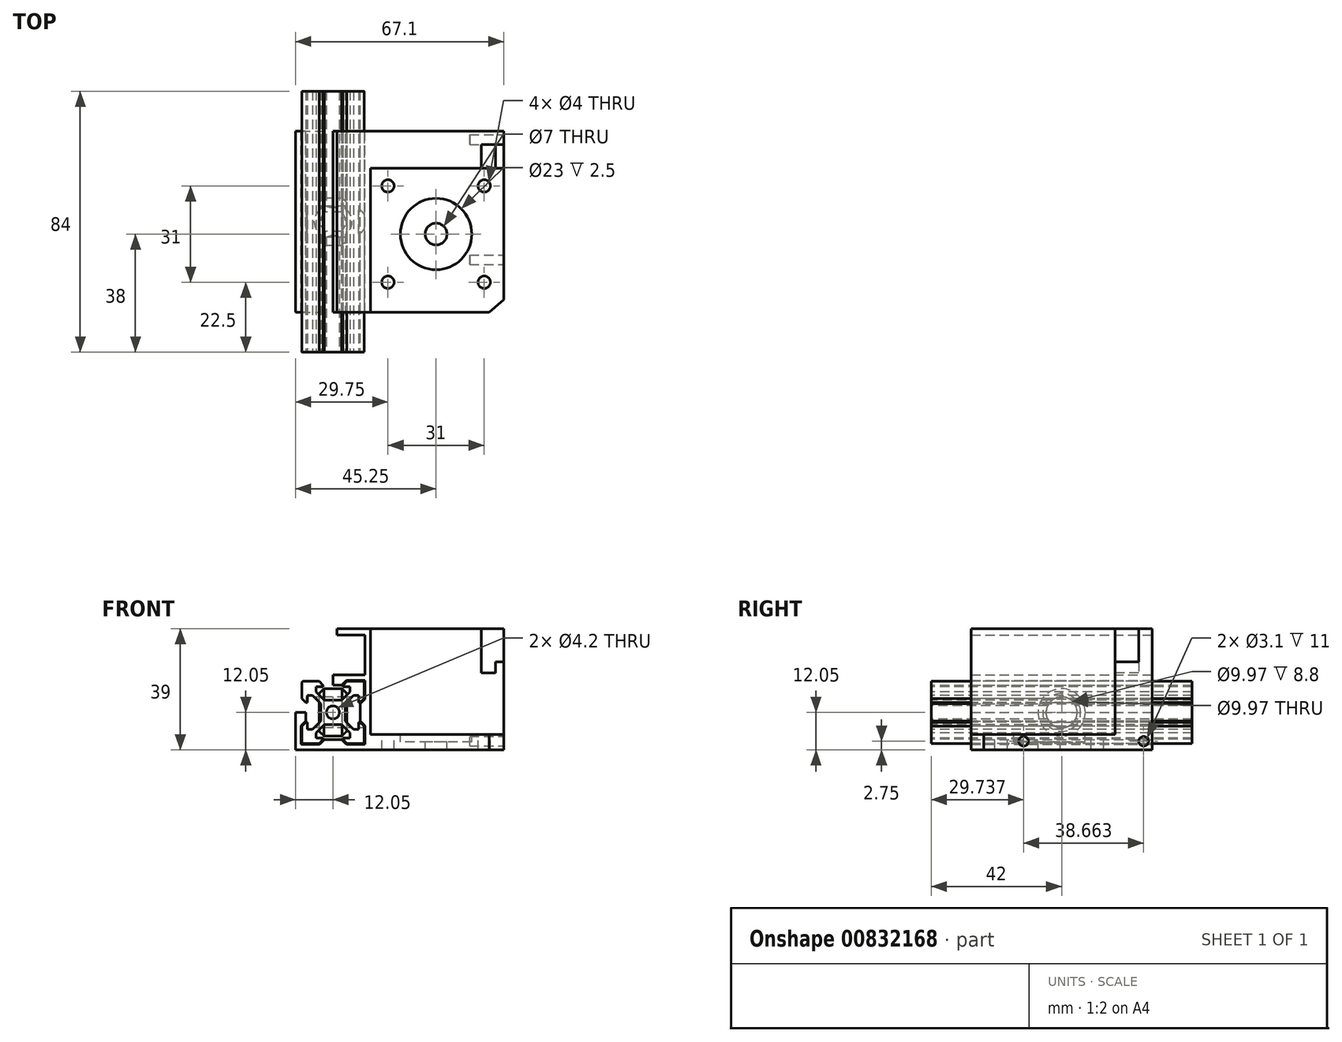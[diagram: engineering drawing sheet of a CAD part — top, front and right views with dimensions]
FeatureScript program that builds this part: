
annotation { "Feature Type Name" : "Feature", "Feature Type Description" : "" }
export const myFeature = defineFeature(function(context is Context, id is Id, definition is map)
    precondition{}
    {
        {
            var Q0;
            Q0=qCreatedBy(makeId("Front.planeOp"),FACE);
            var sketch = newSketch(context, id + "F0", { "sketchPlane" : qUnion([Q0])});
            skLineSegment(sketch, "E0", {"start": v(0, 3.9) * mm, "end": v(-2.84, 3.9) * mm});
            skLineSegment(sketch, "E1", {"start": v(-2.84, 3.9) * mm, "end": v(-5.5, 6.56) * mm});
            skLineSegment(sketch, "E2", {"start": v(-5.5, 6.56) * mm, "end": v(-5.5, 8.2) * mm});
            skLineSegment(sketch, "E3", {"start": v(-5.5, 8.2) * mm, "end": v(-3.15, 8.2) * mm});
            skLineSegment(sketch, "E4", {"start": v(-3.15, 8.7) * mm, "end": v(-4.46, 10) * mm});
            skLineSegment(sketch, "E5", {"start": v(-4.46, 10) * mm, "end": v(-10, 10) * mm});
            skLineSegment(sketch, "E6.MirrorCS", {"start": v(4.46, 10) * mm, "end": v(10, 10) * mm});
            skLineSegment(sketch, "E7.MirrorCS", {"start": v(5.5, 6.56) * mm, "end": v(5.5, 8.2) * mm});
            skLineSegment(sketch, "E8.MirrorCS", {"start": v(2.84, 3.9) * mm, "end": v(5.5, 6.56) * mm});
            skLineSegment(sketch, "E9.MirrorCS", {"start": v(0, 3.9) * mm, "end": v(2.84, 3.9) * mm});
            skLineSegment(sketch, "E10.MirrorCS", {"start": v(-10, 4.46) * mm, "end": v(-10, 10) * mm});
            skLineSegment(sketch, "E11.MirrorCS", {"start": v(-6.56, 5.5) * mm, "end": v(-8.2, 5.5) * mm});
            skLineSegment(sketch, "E12.MirrorCS", {"start": v(-3.9, 2.84) * mm, "end": v(-6.56, 5.5) * mm});
            skLineSegment(sketch, "E13.MirrorCS", {"start": v(10, 4.46) * mm, "end": v(10, 10) * mm});
            skLineSegment(sketch, "E14.MirrorCS", {"start": v(6.56, 5.5) * mm, "end": v(8.2, 5.5) * mm});
            skLineSegment(sketch, "E15.MirrorCS", {"start": v(3.9, 2.84) * mm, "end": v(6.56, 5.5) * mm});
            skLineSegment(sketch, "E16", {"start": v(-3.9, 2.84) * mm, "end": v(-3.9, 0) * mm});
            skLineSegment(sketch, "E17.MirrorCS", {"start": v(3.9, 2.84) * mm, "end": v(3.9, 0) * mm});
            skLineSegment(sketch, "E18.MirrorCS", {"start": v(-3.9, -2.84) * mm, "end": v(-3.9, 0) * mm});
            skLineSegment(sketch, "E19.MirrorCS", {"start": v(-3.9, -2.84) * mm, "end": v(-6.56, -5.5) * mm});
            skLineSegment(sketch, "E20.MirrorCS", {"start": v(-6.56, -5.5) * mm, "end": v(-8.2, -5.5) * mm});
            skLineSegment(sketch, "E21.MirrorCS", {"start": v(-10, -4.46) * mm, "end": v(-10, -10) * mm});
            skLineSegment(sketch, "E22.MirrorCS", {"start": v(-4.46, -10) * mm, "end": v(-10, -10) * mm});
            skLineSegment(sketch, "E23.MirrorCS", {"start": v(-5.5, -6.56) * mm, "end": v(-5.5, -8.2) * mm});
            skLineSegment(sketch, "E24.MirrorCS", {"start": v(-2.84, -3.9) * mm, "end": v(-5.5, -6.56) * mm});
            skLineSegment(sketch, "E25.MirrorCS", {"start": v(0, -3.9) * mm, "end": v(-2.84, -3.9) * mm});
            skLineSegment(sketch, "E26.MirrorCS", {"start": v(0, -3.9) * mm, "end": v(2.84, -3.9) * mm});
            skLineSegment(sketch, "E27.MirrorCS", {"start": v(2.84, -3.9) * mm, "end": v(5.5, -6.56) * mm});
            skLineSegment(sketch, "E28.MirrorCS", {"start": v(5.5, -6.56) * mm, "end": v(5.5, -8.2) * mm});
            skLineSegment(sketch, "E29.MirrorCS", {"start": v(4.46, -10) * mm, "end": v(10, -10) * mm});
            skLineSegment(sketch, "E30.MirrorCS", {"start": v(10, -4.46) * mm, "end": v(10, -10) * mm});
            skLineSegment(sketch, "E31.MirrorCS", {"start": v(6.56, -5.5) * mm, "end": v(8.2, -5.5) * mm});
            skLineSegment(sketch, "E32.MirrorCS", {"start": v(3.9, -2.84) * mm, "end": v(6.56, -5.5) * mm});
            skLineSegment(sketch, "E33.MirrorCS", {"start": v(3.9, -2.84) * mm, "end": v(3.9, 0) * mm});
            skLineSegment(sketch, "E34", {"start": v(-3.15, 8.2) * mm, "end": v(-3.15, 8.7) * mm});
            skPoint(sketch, "E35.MirrorCS.end.orphan", {"position": v(4.46, 10) * mm});
            skPoint(sketch, "E36.MirrorCS.start.orphan", {"position": v(5.5, 8.2) * mm});
            skLineSegment(sketch, "E37.MirrorCS", {"start": v(3.15, 8.7) * mm, "end": v(4.46, 10) * mm});
            skLineSegment(sketch, "E38.MirrorCS", {"start": v(3.15, 8.2) * mm, "end": v(3.15, 8.7) * mm});
            skLineSegment(sketch, "E39.MirrorCS", {"start": v(5.5, 8.2) * mm, "end": v(3.15, 8.2) * mm});
            skLineSegment(sketch, "E40.MirrorCS", {"start": v(-8.7, 3.15) * mm, "end": v(-10, 4.46) * mm});
            skLineSegment(sketch, "E41.MirrorCS", {"start": v(-8.2, 3.15) * mm, "end": v(-8.7, 3.15) * mm});
            skLineSegment(sketch, "E42.MirrorCS", {"start": v(-8.2, 5.5) * mm, "end": v(-8.2, 3.15) * mm});
            skLineSegment(sketch, "E43.MirrorCS", {"start": v(-8.2, -5.5) * mm, "end": v(-8.2, -3.15) * mm});
            skLineSegment(sketch, "E44.MirrorCS", {"start": v(-8.2, -3.15) * mm, "end": v(-8.7, -3.15) * mm});
            skLineSegment(sketch, "E45.MirrorCS", {"start": v(-8.7, -3.15) * mm, "end": v(-10, -4.46) * mm});
            skLineSegment(sketch, "E46.MirrorCS", {"start": v(-5.5, -8.2) * mm, "end": v(-3.15, -8.2) * mm});
            skLineSegment(sketch, "E47.MirrorCS", {"start": v(-3.15, -8.2) * mm, "end": v(-3.15, -8.7) * mm});
            skLineSegment(sketch, "E48.MirrorCS", {"start": v(-3.15, -8.7) * mm, "end": v(-4.46, -10) * mm});
            skLineSegment(sketch, "E49.MirrorCS", {"start": v(8.2, 5.5) * mm, "end": v(8.2, 3.15) * mm});
            skLineSegment(sketch, "E50.MirrorCS", {"start": v(8.2, 3.15) * mm, "end": v(8.7, 3.15) * mm});
            skLineSegment(sketch, "E51.MirrorCS", {"start": v(8.7, 3.15) * mm, "end": v(10, 4.46) * mm});
            skLineSegment(sketch, "E52.MirrorCS", {"start": v(3.15, -8.2) * mm, "end": v(3.15, -8.7) * mm});
            skLineSegment(sketch, "E53.MirrorCS", {"start": v(3.15, -8.7) * mm, "end": v(4.46, -10) * mm});
            skLineSegment(sketch, "E54.MirrorCS", {"start": v(5.5, -8.2) * mm, "end": v(3.15, -8.2) * mm});
            skLineSegment(sketch, "E55.MirrorCS", {"start": v(8.2, -5.5) * mm, "end": v(8.2, -3.15) * mm});
            skLineSegment(sketch, "E56.MirrorCS", {"start": v(8.2, -3.15) * mm, "end": v(8.7, -3.15) * mm});
            skLineSegment(sketch, "E57.MirrorCS", {"start": v(8.7, -3.15) * mm, "end": v(10, -4.46) * mm});
            skCircle(sketch, "E58", {"center": v(0, 0) * mm, "radius": 2.1 * mm});
            skSolve(sketch);
        }
        {
            var Q0;
            Q0=makeQuery(id+"F0.imprint","IMPRINT",FACE,{"disambiguationData":[TD([[makeQuery(id+"F0.imprint","IMPRINT",EDGE,{"derivedFrom":sQuery(id+"F0.wireOp",EDGE,"E0")}),1.0]])]});
            extrude(context, id + "F1", {"entities" : qUnion([Q0]), "endBound" : BoundingType.SYMMETRIC, "oppositeDirection" : true, "depth" : 84 * mm, "offsetDistance" : 25 * mm});
        }
        {
            var Q0;
            Q0=makeQuery(id+"F1.opExtrude","SWEPT_EDGE",EDGE,{"disambiguationData":[OSD([sQuery(id+"F0.wireOp",EDGE,"E6.MirrorCS"),sQuery(id+"F0.wireOp",EDGE,"E13.MirrorCS")])]});
            var Q1;
            Q1=makeQuery(id+"F1.opExtrude","SWEPT_EDGE",EDGE,{"disambiguationData":[OSD([sQuery(id+"F0.wireOp",EDGE,"E5"),sQuery(id+"F0.wireOp",EDGE,"E10.MirrorCS")])]});
            var Q2;
            Q2=makeQuery(id+"F1.opExtrude","SWEPT_EDGE",EDGE,{"disambiguationData":[OSD([sQuery(id+"F0.wireOp",EDGE,"E29.MirrorCS"),sQuery(id+"F0.wireOp",EDGE,"E30.MirrorCS")])]});
            var Q3;
            Q3=makeQuery(id+"F1.opExtrude","SWEPT_EDGE",EDGE,{"disambiguationData":[OSD([sQuery(id+"F0.wireOp",EDGE,"E21.MirrorCS"),sQuery(id+"F0.wireOp",EDGE,"E22.MirrorCS")])]});
            fillet(context, id + "F2", {"entities" : qUnion([Q0, Q1, Q2, Q3]), "radius" : .5 * mm, "tangentPropagation" : true, "allowEdgeOverflow" : false});
        }
        {
            var Q0;
            Q0=qCreatedBy(makeId("Front.planeOp"),FACE);
            var sketch = newSketch(context, id + "F3", { "sketchPlane" : qUnion([Q0])});
            skLineSegment(sketch, "E59.bottom", {"start": v(2.89, -7.62) * mm, "end": v(-2.89, -7.61) * mm});
            skLineSegment(sketch, "E59.top", {"start": v(2.89, 7.61) * mm, "end": v(-2.89, 7.62) * mm});
            skLineSegment(sketch, "E59.left", {"start": v(4.4, -6.1) * mm, "end": v(4.4, 6.1) * mm});
            skLineSegment(sketch, "E59.right", {"start": v(-4.4, -6.1) * mm, "end": v(-4.4, 6.1) * mm});
            skPoint(sketch, "E59.middle", {"position": v(0, 0) * mm});
            skLineSegment(sketch, "E60", {"start": v(-4.4, 6.1) * mm, "end": v(-2.89, 7.62) * mm});
            skLineSegment(sketch, "E61.MirrorCS", {"start": v(4.4, 6.1) * mm, "end": v(2.89, 7.62) * mm});
            skLineSegment(sketch, "E62.MirrorCS", {"start": v(-4.4, -6.1) * mm, "end": v(-2.89, -7.62) * mm});
            skLineSegment(sketch, "E63.MirrorCS", {"start": v(4.4, -6.1) * mm, "end": v(2.89, -7.62) * mm});
            skLineSegment(sketch, "E64", {"start": v(-4.4, 0) * mm, "end": v(0, 0) * mm});
            skLineSegment(sketch, "E65", {"start": v(4.4, 0) * mm, "end": v(0, 0) * mm});
            skSolve(sketch);
        }
        {
            var Q0;
            Q0=makeQuery(id+"F3.imprint","IMPRINT",FACE,{"disambiguationData":[TD([[makeQuery(id+"F3.imprint","IMPRINT",EDGE,{"derivedFrom":sQuery(id+"F3.wireOp",EDGE,"E59.top")}),1.0]])]});
            var Q1;
            Q1=sQuery(id+"F3.wireOp",EDGE,"E65");
            revolve(context, id + "F4", {"surfaceOperationType" : NewSurfaceOperationType.NEW, "entities" : qUnion([Q0]), "axis" : qUnion([Q1]), "revolveType" : RevolveType.FULL});
        }
        {
            var Q0;
            Q0=makeQuery(id+"F4.opRevolve","SWEPT_FACE",FACE,{"disambiguationData":[OSD([sQuery(id+"F3.wireOp",EDGE,"E59.left")])]});
            var sketch = newSketch(context, id + "F5", { "sketchPlane" : qUnion([Q0])});
            skCircle(sketch, "E66", {"center": v(0, 0) * mm, "radius": 4.99 * mm});
            skSolve(sketch);
        }
        {
            var Q0;
            Q0=makeQuery(id+"F5.imprint","IMPRINT",FACE,{"disambiguationData":[TD([[makeQuery(id+"F5.imprint","IMPRINT",EDGE,{"derivedFrom":sQuery(id+"F5.wireOp",EDGE,"E66")}),1.0]])]});
            var Q1;
            Q1=sQuery(id+"F5.wireOp",EDGE,"E66");
            extrude(context, id + "F6", {"entities" : qUnion([Q0]), "operationType" : NewBodyOperationType.REMOVE, "surfaceEntities" : qUnion([Q1]), "endBound" : BoundingType.SYMMETRIC, "depth" : 25.8 * mm, "offsetDistance" : 25 * mm});
        }
        {
            var Q0;
            Q0=qCreatedBy(makeId("Front.planeOp"),FACE);
            var sketch = newSketch(context, id + "F7", { "sketchPlane" : qUnion([Q0])});
            skLineSegment(sketch, "E67", {"start": v(-4.33, -10.3) * mm, "end": v(-2.83, -8.8) * mm});
            skLineSegment(sketch, "E68", {"start": v(-2.83, -8.8) * mm, "end": v(0, -8.8) * mm});
            skLineSegment(sketch, "E69", {"start": v(0, -8.8) * mm, "end": v(0, -12.05) * mm});
            skLineSegment(sketch, "E70", {"start": v(0, -12.05) * mm, "end": v(-12.05, -12.05) * mm});
            skLineSegment(sketch, "E71", {"start": v(-12.05, -12.05) * mm, "end": v(-12.05, 0) * mm});
            skLineSegment(sketch, "E72", {"start": v(-12.05, 0) * mm, "end": v(-8.8, 0) * mm});
            skLineSegment(sketch, "E73", {"start": v(-8.8, 0) * mm, "end": v(-8.8, -2.83) * mm});
            skLineSegment(sketch, "E74", {"start": v(-8.8, -2.83) * mm, "end": v(-10.3, -4.33) * mm});
            skLineSegment(sketch, "E75", {"start": v(-10.3, -4.33) * mm, "end": v(-10.3, -10.3) * mm});
            skLineSegment(sketch, "E76", {"start": v(-10.3, -10.3) * mm, "end": v(-4.33, -10.3) * mm});
            skLineSegment(sketch, "E77.MirrorCS", {"start": v(0, -12.05) * mm, "end": v(12.05, -12.05) * mm});
            skLineSegment(sketch, "E78.MirrorCS", {"start": v(2.83, -8.8) * mm, "end": v(0, -8.8) * mm});
            skLineSegment(sketch, "E79.MirrorCS", {"start": v(4.33, -10.3) * mm, "end": v(2.83, -8.8) * mm});
            skLineSegment(sketch, "E80.MirrorCS", {"start": v(10.3, -10.3) * mm, "end": v(4.33, -10.3) * mm});
            skLineSegment(sketch, "E81.MirrorCS", {"start": v(10.3, -4.33) * mm, "end": v(10.3, -10.3) * mm});
            skLineSegment(sketch, "E82.MirrorCS", {"start": v(12.05, -12.05) * mm, "end": v(12.05, 0) * mm});
            skLineSegment(sketch, "E83.MirrorCS", {"start": v(12.05, 0) * mm, "end": v(8.8, 0) * mm});
            skLineSegment(sketch, "E84.MirrorCS", {"start": v(8.8, 0) * mm, "end": v(8.8, -2.83) * mm});
            skLineSegment(sketch, "E85.MirrorCS", {"start": v(12.05, 12.05) * mm, "end": v(12.05, 0) * mm});
            skLineSegment(sketch, "E86.MirrorCS", {"start": v(8.8, -2.83) * mm, "end": v(10.3, -4.33) * mm});
            skLineSegment(sketch, "E87.MirrorCS", {"start": v(8.8, 0) * mm, "end": v(8.8, 2.83) * mm});
            skLineSegment(sketch, "E88.MirrorCS", {"start": v(8.8, 2.83) * mm, "end": v(10.3, 4.33) * mm});
            skLineSegment(sketch, "E89.MirrorCS", {"start": v(10.3, 4.33) * mm, "end": v(10.3, 10.3) * mm});
            skLineSegment(sketch, "E90.MirrorCS", {"start": v(10.3, 10.3) * mm, "end": v(4.33, 10.3) * mm});
            skLineSegment(sketch, "E91.MirrorCS", {"start": v(4.33, 10.3) * mm, "end": v(2.83, 8.8) * mm});
            skLineSegment(sketch, "E92.MirrorCS", {"start": v(2.83, 8.8) * mm, "end": v(0, 8.8) * mm});
            skLineSegment(sketch, "E93.MirrorCS", {"start": v(0, 8.8) * mm, "end": v(0, 12.05) * mm});
            skLineSegment(sketch, "E94.MirrorCS", {"start": v(0, 12.05) * mm, "end": v(12.05, 12.05) * mm});
            skLineSegment(sketch, "E95", {"start": v(10.3, 12.05) * mm, "end": v(10.3, 26.95) * mm});
            skLineSegment(sketch, "E96", {"start": v(12.05, 12.05) * mm, "end": v(12.05, 26.95) * mm});
            skLineSegment(sketch, "E97", {"start": v(12.05, 26.95) * mm, "end": v(10.3, 26.95) * mm});
            skLineSegment(sketch, "E98", {"start": v(12.05, -12.05) * mm, "end": v(55.05, -12.05) * mm});
            skLineSegment(sketch, "E99", {"start": v(55.05, -12.05) * mm, "end": v(55.05, -7.05) * mm});
            skLineSegment(sketch, "E100", {"start": v(55.05, -7.05) * mm, "end": v(12.05, -7.05) * mm});
            skLineSegment(sketch, "E101", {"start": v(10.3, 26.95) * mm, "end": v(1.3, 26.95) * mm});
            skLineSegment(sketch, "E102", {"start": v(1.3, 26.95) * mm, "end": v(1.3, 24.95) * mm});
            skLineSegment(sketch, "E103", {"start": v(1.3, 24.95) * mm, "end": v(10.3, 24.95) * mm});
            skLineSegment(sketch, "E104", {"start": v(12.05, 26.95) * mm, "end": v(47.8, 26.95) * mm});
            skLineSegment(sketch, "E105", {"start": v(55.05, 26.95) * mm, "end": v(55.05, 16.25) * mm});
            skLineSegment(sketch, "E106", {"start": v(47.8, 26.95) * mm, "end": v(47.8, 12.75) * mm});
            skLineSegment(sketch, "E107", {"start": v(47.8, 12.75) * mm, "end": v(52.3, 12.75) * mm});
            skLineSegment(sketch, "E108", {"start": v(55.05, 16.25) * mm, "end": v(52.3, 16.25) * mm});
            skLineSegment(sketch, "E109", {"start": v(52.3, 16.25) * mm, "end": v(52.3, 12.75) * mm});
            skLineSegment(sketch, "E110", {"start": v(47.8, 26.95) * mm, "end": v(55.05, 26.95) * mm});
            skLineSegment(sketch, "E111", {"start": v(55.05, 16.25) * mm, "end": v(55.05, -7.05) * mm});
            skLineSegment(sketch, "E112", {"start": v(52.3, 12.75) * mm, "end": v(55.05, 12.75) * mm});
            skSolve(sketch);
        }
        {
            var Q0;
            Q0=makeQuery(id+"F7.imprint","IMPRINT",FACE,{"disambiguationData":[TD([[makeQuery(id+"F7.imprint","IMPRINT",EDGE,{"derivedFrom":sQuery(id+"F7.wireOp",EDGE,"E83.MirrorCS")}),-1.0]])]});
            var Q1;
            Q1=makeQuery(id+"F7.imprint","IMPRINT",FACE,{"disambiguationData":[TD([[makeQuery(id+"F7.imprint","IMPRINT",EDGE,{"derivedFrom":sQuery(id+"F7.wireOp",EDGE,"E69")}),1.0]])]});
            var Q2;
            Q2=makeQuery(id+"F7.imprint","IMPRINT",FACE,{"disambiguationData":[TD([[makeQuery(id+"F7.imprint","IMPRINT",EDGE,{"derivedFrom":sQuery(id+"F7.wireOp",EDGE,"E67")}),-1.0]])]});
            var Q3;
            {var subQ0=sQuery(id+"F7.wireOp",EDGE,"E96");Q3=makeQuery(id+"F7.imprint","IMPRINT",FACE,{"disambiguationData":[TD([[makeQuery(id+"F7.imprint","IMPRINT",EDGE,{"derivedFrom":subQ0}),1.0]])]});}
            var Q4;
            {var subQ0=sQuery(id+"F7.wireOp",EDGE,"E101");Q4=makeQuery(id+"F7.imprint","IMPRINT",FACE,{"disambiguationData":[TD([[makeQuery(id+"F7.imprint","IMPRINT",EDGE,{"derivedFrom":subQ0}),1.0]])]});}
            var Q5;
            {var subQ0=sQuery(id+"F7.wireOp",EDGE,"E98");Q5=makeQuery(id+"F7.imprint","IMPRINT",FACE,{"disambiguationData":[TD([[makeQuery(id+"F7.imprint","IMPRINT",EDGE,{"derivedFrom":subQ0}),1.0]])]});}
            extrude(context, id + "F8", {"entities" : qUnion([Q0, Q1, Q2, Q3, Q4, Q5]), "endBound" : BoundingType.SYMMETRIC, "depth" : 58.3 * mm, "offsetDistance" : 25 * mm});
        }
        {
            var Q0;
            Q0=qCreatedBy(makeId("Right.planeOp"),FACE);
            var sketch = newSketch(context, id + "F9", { "sketchPlane" : qUnion([Q0])});
            skLineSegment(sketch, "E113", {"start": v(29.15, 26.95) * mm, "end": v(17.15, 26.95) * mm});
            skLineSegment(sketch, "E114", {"start": v(17.15, 26.95) * mm, "end": v(17.15, -7.05) * mm});
            skLineSegment(sketch, "E115", {"start": v(17.15, -7.05) * mm, "end": v(29.15, -7.05) * mm});
            skLineSegment(sketch, "E116", {"start": v(29.15, -7.05) * mm, "end": v(29.15, 26.95) * mm});
            skSolve(sketch);
        }
        {
            var Q0;
            Q0=makeQuery(id+"F9.imprint","IMPRINT",FACE,{"disambiguationData":[TD([[makeQuery(id+"F9.imprint","IMPRINT",EDGE,{"derivedFrom":sQuery(id+"F9.wireOp",EDGE,"E113")}),1.0]])]});
            extrude(context, id + "F10", {"entities" : qUnion([Q0]), "operationType" : NewBodyOperationType.ADD, "depth" : 55.05 * mm, "offsetDistance" : 25 * mm, "hasSecondDirection" : true, "secondDirectionOppositeDirection" : false, "secondDirectionDepth" : 12 * mm});
        }
        {
            var Q0;
            Q0=qCreatedBy(makeId("Top.planeOp"),FACE);
            var sketch = newSketch(context, id + "F11", { "sketchPlane" : qUnion([Q0])});
            skCircle(sketch, "E117", {"center": v(33.2, -4) * mm, "radius": 3.5 * mm});
            skCircle(sketch, "E118", {"center": v(33.2, -4) * mm, "radius": 11.5 * mm});
            skCircle(sketch, "E119", {"center": v(17.7, 11.5) * mm, "radius": 2 * mm});
            skCircle(sketch, "E120", {"center": v(48.7, 11.5) * mm, "radius": 2 * mm});
            skCircle(sketch, "E121", {"center": v(48.7, -19.5) * mm, "radius": 2 * mm});
            skCircle(sketch, "E122", {"center": v(17.7, -19.5) * mm, "radius": 2 * mm});
            skSolve(sketch);
        }
        {
            var Q0;
            Q0=sQuery(id+"F11.wireOp",VERTEX,"E122.center");
            var Q1;
            Q1=sQuery(id+"F11.wireOp",VERTEX,"E121.center");
            var Q2;
            Q2=sQuery(id+"F11.wireOp",VERTEX,"E120.center");
            var Q3;
            Q3=sQuery(id+"F11.wireOp",VERTEX,"E119.center");
            var Q4;
            Q4=makeQuery(id+"F8.opExtrude","SWEPT_BODY",BODY,{"disambiguationData":[OSD([sQuery(id+"F7.wireOp",EDGE,"E67"),sQuery(id+"F7.wireOp",EDGE,"E68"),sQuery(id+"F7.wireOp",EDGE,"E70"),sQuery(id+"F7.wireOp",EDGE,"E71"),sQuery(id+"F7.wireOp",EDGE,"E72"),sQuery(id+"F7.wireOp",EDGE,"E73"),sQuery(id+"F7.wireOp",EDGE,"E74"),sQuery(id+"F7.wireOp",EDGE,"E75"),sQuery(id+"F7.wireOp",EDGE,"E76"),sQuery(id+"F7.wireOp",EDGE,"E77.MirrorCS"),sQuery(id+"F7.wireOp",EDGE,"E78.MirrorCS"),sQuery(id+"F7.wireOp",EDGE,"E79.MirrorCS"),sQuery(id+"F7.wireOp",EDGE,"E80.MirrorCS"),sQuery(id+"F7.wireOp",EDGE,"E81.MirrorCS"),sQuery(id+"F7.wireOp",EDGE,"E82.MirrorCS"),sQuery(id+"F7.wireOp",EDGE,"E84.MirrorCS"),sQuery(id+"F7.wireOp",EDGE,"E85.MirrorCS"),sQuery(id+"F7.wireOp",EDGE,"E86.MirrorCS"),sQuery(id+"F7.wireOp",EDGE,"E87.MirrorCS"),sQuery(id+"F7.wireOp",EDGE,"E88.MirrorCS"),sQuery(id+"F7.wireOp",EDGE,"E89.MirrorCS"),sQuery(id+"F7.wireOp",EDGE,"E90.MirrorCS"),sQuery(id+"F7.wireOp",EDGE,"E91.MirrorCS"),sQuery(id+"F7.wireOp",EDGE,"E92.MirrorCS"),sQuery(id+"F7.wireOp",EDGE,"E93.MirrorCS"),sQuery(id+"F7.wireOp",EDGE,"E94.MirrorCS"),sQuery(id+"F7.wireOp",EDGE,"E95"),sQuery(id+"F7.wireOp",EDGE,"E96"),sQuery(id+"F7.wireOp",EDGE,"E97"),sQuery(id+"F7.wireOp",EDGE,"E98"),sQuery(id+"F7.wireOp",EDGE,"E99"),sQuery(id+"F7.wireOp",EDGE,"E100"),sQuery(id+"F7.wireOp",EDGE,"E101"),sQuery(id+"F7.wireOp",EDGE,"E102"),sQuery(id+"F7.wireOp",EDGE,"E103")])]});
            hole(context, id + "F12", {"style" : HoleStyle.SIMPLE, "endStyle" : HoleEndStyle.THROUGH, "holeDiameter" : 4 * mm, "majorDiameter" : 5 * mm, "isTappedThrough" : true, "tappedDepth" : 12 * mm, "tapClearance" : 3, "locations" : qUnion([Q0, Q1, Q2, Q3]), "scope" : qUnion([Q4])});
        }
        {
            var Q0;
            Q0=sQuery(id+"F11.wireOp",VERTEX,"E117.center");
            var Q1;
            Q1=makeQuery(id+"F8.opExtrude","SWEPT_BODY",BODY,{"disambiguationData":[OSD([sQuery(id+"F7.wireOp",EDGE,"E67"),sQuery(id+"F7.wireOp",EDGE,"E68"),sQuery(id+"F7.wireOp",EDGE,"E70"),sQuery(id+"F7.wireOp",EDGE,"E71"),sQuery(id+"F7.wireOp",EDGE,"E72"),sQuery(id+"F7.wireOp",EDGE,"E73"),sQuery(id+"F7.wireOp",EDGE,"E74"),sQuery(id+"F7.wireOp",EDGE,"E75"),sQuery(id+"F7.wireOp",EDGE,"E76"),sQuery(id+"F7.wireOp",EDGE,"E77.MirrorCS"),sQuery(id+"F7.wireOp",EDGE,"E78.MirrorCS"),sQuery(id+"F7.wireOp",EDGE,"E79.MirrorCS"),sQuery(id+"F7.wireOp",EDGE,"E80.MirrorCS"),sQuery(id+"F7.wireOp",EDGE,"E81.MirrorCS"),sQuery(id+"F7.wireOp",EDGE,"E82.MirrorCS"),sQuery(id+"F7.wireOp",EDGE,"E84.MirrorCS"),sQuery(id+"F7.wireOp",EDGE,"E85.MirrorCS"),sQuery(id+"F7.wireOp",EDGE,"E86.MirrorCS"),sQuery(id+"F7.wireOp",EDGE,"E87.MirrorCS"),sQuery(id+"F7.wireOp",EDGE,"E88.MirrorCS"),sQuery(id+"F7.wireOp",EDGE,"E89.MirrorCS"),sQuery(id+"F7.wireOp",EDGE,"E90.MirrorCS"),sQuery(id+"F7.wireOp",EDGE,"E91.MirrorCS"),sQuery(id+"F7.wireOp",EDGE,"E92.MirrorCS"),sQuery(id+"F7.wireOp",EDGE,"E93.MirrorCS"),sQuery(id+"F7.wireOp",EDGE,"E94.MirrorCS"),sQuery(id+"F7.wireOp",EDGE,"E95"),sQuery(id+"F7.wireOp",EDGE,"E96"),sQuery(id+"F7.wireOp",EDGE,"E97"),sQuery(id+"F7.wireOp",EDGE,"E98"),sQuery(id+"F7.wireOp",EDGE,"E99"),sQuery(id+"F7.wireOp",EDGE,"E100"),sQuery(id+"F7.wireOp",EDGE,"E101"),sQuery(id+"F7.wireOp",EDGE,"E102"),sQuery(id+"F7.wireOp",EDGE,"E103")])]});
            hole(context, id + "F13", {"style" : HoleStyle.C_BORE, "endStyle" : HoleEndStyle.THROUGH, "holeDiameter" : 7 * mm, "cBoreDiameter" : 23 * mm, "cBoreDepth" : 2.5 * mm, "majorDiameter" : 5 * mm, "isTappedThrough" : true, "tappedDepth" : 12 * mm, "tapClearance" : 3, "locations" : qUnion([Q0]), "scope" : qUnion([Q1])});
        }
        {
            var Q0;
            Q0=makeQuery(id+"F10.opExtrude","SWEPT_FACE",FACE,{"disambiguationData":[OSD([sQuery(id+"F9.wireOp",EDGE,"E114")])]});
            var sketch = newSketch(context, id + "F14", { "sketchPlane" : qUnion([Q0])});
            skLineSegment(sketch, "E123", {"start": v(47.8, 26.95) * mm, "end": v(47.8, 12.75) * mm});
            skLineSegment(sketch, "E124", {"start": v(47.8, 12.75) * mm, "end": v(52.3, 12.75) * mm});
            skLineSegment(sketch, "E125", {"start": v(52.3, 12.75) * mm, "end": v(52.3, 16.25) * mm});
            skLineSegment(sketch, "E126", {"start": v(52.3, 16.25) * mm, "end": v(55.05, 16.25) * mm});
            skLineSegment(sketch, "E127", {"start": v(55.05, 16.25) * mm, "end": v(55.05, 26.95) * mm});
            skLineSegment(sketch, "E128", {"start": v(55.05, 26.95) * mm, "end": v(47.8, 26.95) * mm});
            skSolve(sketch);
        }
        {
            var Q0;
            Q0=makeQuery(id+"F14.imprint","IMPRINT",FACE,{"disambiguationData":[TD([[makeQuery(id+"F14.imprint","IMPRINT",EDGE,{"derivedFrom":sQuery(id+"F14.wireOp",EDGE,"E123")}),1.0]])]});
            extrude(context, id + "F15", {"entities" : qUnion([Q0]), "operationType" : NewBodyOperationType.REMOVE, "depth" : 0 * mm, "offsetDistance" : 25 * mm, "hasSecondDirection" : true, "secondDirectionOppositeDirection" : true, "secondDirectionDepth" : 7.67 * mm});
        }
        {
            var Q0;
            Q0=makeQuery(id+"F10.boolean.opBoolean","MERGE",FACE,{"derivedFrom":[makeQuery(id+"F8.opExtrude","SWEPT_FACE",FACE,{"disambiguationData":[OSD([sQuery(id+"F7.wireOp",EDGE,"E99")])]}),makeQuery(id+"F10.opExtrude","CAP_FACE",FACE,{"disambiguationData":[OSD([sQuery(id+"F9.wireOp",EDGE,"E113"),sQuery(id+"F9.wireOp",EDGE,"E114"),sQuery(id+"F9.wireOp",EDGE,"E115"),sQuery(id+"F9.wireOp",EDGE,"E116")])],"isStart":false})]});
            var sketch = newSketch(context, id + "F16", { "sketchPlane" : qUnion([Q0])});
            skCircle(sketch, "E129", {"center": v(-12.26, -9.3) * mm, "radius": 1.55 * mm});
            skCircle(sketch, "E130", {"center": v(26.4, -9.3) * mm, "radius": 1.55 * mm});
            skSolve(sketch);
        }
        {
            var Q0;
            Q0=makeQuery(id+"F16.imprint","IMPRINT",FACE,{"disambiguationData":[TD([[makeQuery(id+"F16.imprint","IMPRINT",EDGE,{"derivedFrom":sQuery(id+"F16.wireOp",EDGE,"E129")}),1.0]])]});
            var Q1;
            Q1=makeQuery(id+"F16.imprint","IMPRINT",FACE,{"disambiguationData":[TD([[makeQuery(id+"F16.imprint","IMPRINT",EDGE,{"derivedFrom":sQuery(id+"F16.wireOp",EDGE,"E130")}),1.0]])]});
            var Q2;
            Q2=sQuery(id+"F16.wireOp",EDGE,"E129");
            var Q3;
            Q3=sQuery(id+"F16.wireOp",EDGE,"E130");
            extrude(context, id + "F17", {"entities" : qUnion([Q0, Q1]), "operationType" : NewBodyOperationType.REMOVE, "surfaceEntities" : qUnion([Q2, Q3]), "oppositeDirection" : true, "depth" : 11 * mm, "offsetDistance" : 25 * mm});
        }
        {
            var Q0;
            Q0=makeQuery(id+"F8.opExtrude","SWEPT_FACE",FACE,{"disambiguationData":[OSD([sQuery(id+"F7.wireOp",EDGE,"E100")])]});
            var sketch = newSketch(context, id + "F18", { "sketchPlane" : qUnion([Q0])});
            skLineSegment(sketch, "E131", {"start": v(50.33, -29.15) * mm, "end": v(55.05, -25.13) * mm});
            skLineSegment(sketch, "E132", {"start": v(55.05, -25.13) * mm, "end": v(55.05, -29.15) * mm});
            skLineSegment(sketch, "E133", {"start": v(55.05, -29.15) * mm, "end": v(50.33, -29.15) * mm});
            skSolve(sketch);
        }
        {
            var Q0;
            Q0=makeQuery(id+"F18.imprint","IMPRINT",FACE,{"disambiguationData":[TD([[makeQuery(id+"F18.imprint","IMPRINT",EDGE,{"derivedFrom":sQuery(id+"F18.wireOp",EDGE,"E131")}),-1.0]])]});
            extrude(context, id + "F19", {"entities" : qUnion([Q0]), "operationType" : NewBodyOperationType.REMOVE, "endBound" : BoundingType.UP_TO_NEXT, "oppositeDirection" : true, "depth" : 25 * mm, "offsetDistance" : 25 * mm});
        }
    });
